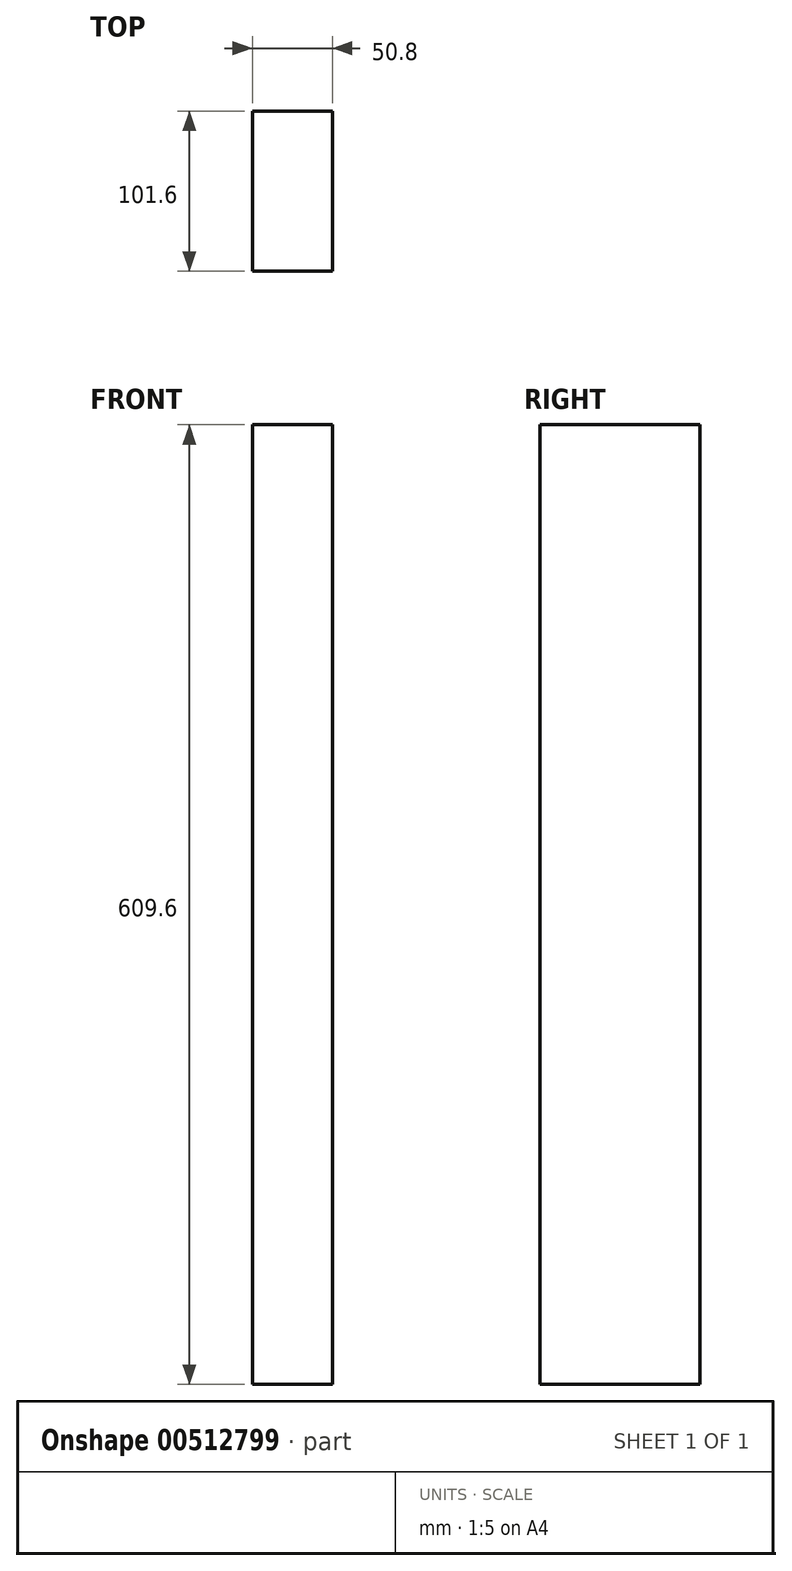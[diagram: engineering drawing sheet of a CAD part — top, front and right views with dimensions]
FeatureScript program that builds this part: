
annotation { "Feature Type Name" : "Feature", "Feature Type Description" : "" }
export const myFeature = defineFeature(function(context is Context, id is Id, definition is map)
    precondition{}
    {
        {
            var Q0;
            Q0=qCreatedBy(makeId("Top.planeOp"),FACE);
            var sketch = newSketch(context, id + "F0", { "sketchPlane" : qUnion([Q0])});
            skLineSegment(sketch, "E0.bottom", {"start": v(25.4, 50.8) * mm, "end": v(-25.4, 50.8) * mm});
            skLineSegment(sketch, "E0.top", {"start": v(25.4, -50.8) * mm, "end": v(-25.4, -50.8) * mm});
            skLineSegment(sketch, "E0.left", {"start": v(25.4, 50.8) * mm, "end": v(25.4, -50.8) * mm});
            skLineSegment(sketch, "E0.right", {"start": v(-25.4, 50.8) * mm, "end": v(-25.4, -50.8) * mm});
            skPoint(sketch, "E0.middle", {"position": v(0, 0) * mm});
            skSolve(sketch);
        }
        {
            var Q0;
            Q0=makeQuery(id+"F0.imprint","IMPRINT",FACE,{"disambiguationData":[TD([[makeQuery(id+"F0.imprint","IMPRINT",EDGE,{"derivedFrom":sQuery(id+"F0.wireOp",EDGE,"E0.bottom")}),1.0]])]});
            extrude(context, id + "F1", {"entities" : qUnion([Q0]), "depth" : 609.6 * mm});
        }
    });
